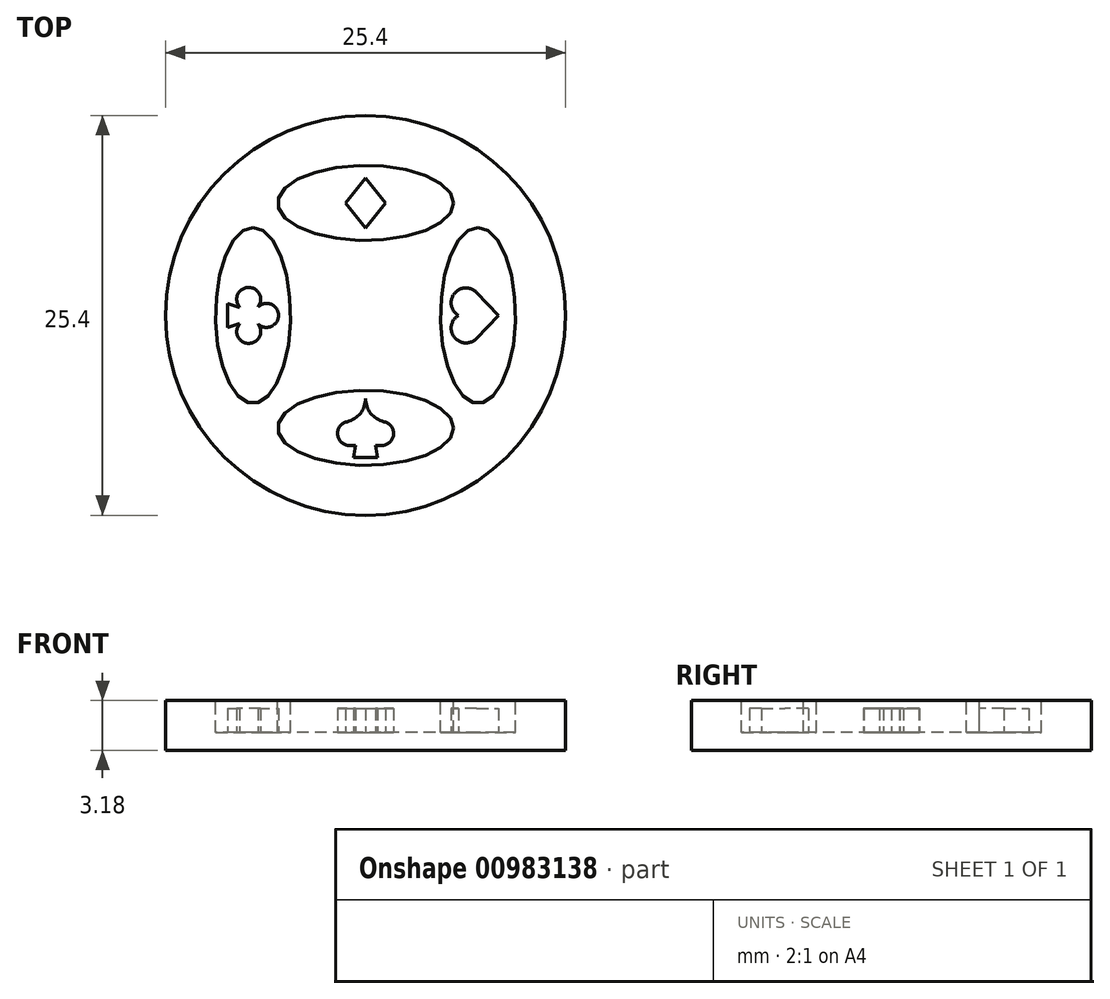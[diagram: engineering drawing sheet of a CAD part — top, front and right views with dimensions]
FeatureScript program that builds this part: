
annotation { "Feature Type Name" : "Feature", "Feature Type Description" : "" }
export const myFeature = defineFeature(function(context is Context, id is Id, definition is map)
    precondition{}
    {
        {
            var Q0;
            Q0=qCreatedBy(makeId("Top.planeOp"),FACE);
            var sketch = newSketch(context, id + "F0", { "sketchPlane" : qUnion([Q0])});
            skCircle(sketch, "E0", {"center": v(0, 0) * mm, "radius": 12.7 * mm});
            skSolve(sketch);
        }
        {
            var Q0;
            Q0 = qSketchRegion(id + "F0", true);
            extrude(context, id + "F1", {"entities" : qUnion([Q0]), "endBound" : BoundingType.SYMMETRIC, "depth" : 3.17 * mm, "offsetDistance" : 25.4 * mm});
        }
        {
            var Q0;
            Q0=makeQuery(id+"F1.opExtrude","CAP_FACE",FACE,{"disambiguationData":[OSD([sQuery(id+"F0.wireOp",EDGE,"E0")])],"isStart":false});
            var sketch = newSketch(context, id + "F2", { "sketchPlane" : qUnion([Q0])});
            skEllipse(sketch, "E1", {"center": v(0, 7.14) * mm, "majorRadius": 5.59 * mm, "minorRadius": 2.38 * mm, "majorAxis": v(1, 0)});
            skEllipse(sketch, "E2", {"center": v(7.14, 0) * mm, "majorRadius": 2.38 * mm, "minorRadius": 5.59 * mm, "majorAxis": v(1, 0)});
            skEllipse(sketch, "E3", {"center": v(0, -7.14) * mm, "majorRadius": 5.59 * mm, "minorRadius": 2.38 * mm, "majorAxis": v(1, 0)});
            skLineSegment(sketch, "E4", {"start": v(0, 4.76) * mm, "end": v(0, 9.52) * mm, "construction": true});
            skLineSegment(sketch, "E5", {"start": v(5.59, 7.14) * mm, "end": v(-5.59, 7.14) * mm, "construction": true});
            skPoint(sketch, "E6.endSnap0", {"position": v(-5.59, -7.14) * mm});
            skLineSegment(sketch, "E7", {"start": v(5.59, 7.14) * mm, "end": v(5.59, -7.14) * mm, "construction": true});
            skPoint(sketch, "E8.endSnap0", {"position": v(7.14, -5.59) * mm});
            skLineSegment(sketch, "E9", {"start": v(4.76, 0) * mm, "end": v(9.53, 0) * mm, "construction": true});
            skLineSegment(sketch, "E10", {"start": v(7.14, 5.59) * mm, "end": v(7.14, -5.59) * mm, "construction": true});
            skLineSegment(sketch, "E11", {"start": v(-5.59, -7.14) * mm, "end": v(5.59, -7.14) * mm, "construction": true});
            skLineSegment(sketch, "E12", {"start": v(0, -4.76) * mm, "end": v(0, -9.52) * mm, "construction": true});
            skEllipse(sketch, "E13", {"center": v(-7.14, 0) * mm, "majorRadius": 2.38 * mm, "minorRadius": 5.59 * mm, "majorAxis": v(1, 0)});
            skLineSegment(sketch, "E14", {"start": v(-7.14, 5.59) * mm, "end": v(-7.14, -5.59) * mm, "construction": true});
            skLineSegment(sketch, "E15", {"start": v(-4.76, 0) * mm, "end": v(-9.52, 0) * mm, "construction": true});
            skLineSegment(sketch, "E16", {"start": v(-7.14, 5.59) * mm, "end": v(7.14, 5.59) * mm, "construction": true});
            skLineSegment(sketch, "E17", {"start": v(0, 5.59) * mm, "end": v(0, 4.76) * mm, "construction": true});
            skLineSegment(sketch, "E18", {"start": v(5.59, 0) * mm, "end": v(4.76, 0) * mm, "construction": true});
            skSolve(sketch);
        }
        {
            var Q0;
            Q0 = qSketchRegion(id + "F2", true);
            extrude(context, id + "F3", {"entities" : qUnion([Q0]), "operationType" : NewBodyOperationType.REMOVE, "oppositeDirection" : true, "depth" : 2.03 * mm, "offsetDistance" : 25.4 * mm});
        }
        {
            var Q0;
            Q0=makeQuery(id+"F3.boolean.opBoolean","COPY",FACE,{"derivedFrom":makeQuery(id+"F3.opExtrude","CAP_FACE",FACE,{"disambiguationData":[OSD([sQuery(id+"F2.wireOp",EDGE,"E1")])],"isStart":false})});
            var sketch = newSketch(context, id + "F4", { "sketchPlane" : qUnion([Q0])});
            skPoint(sketch, "E19.firstSnap0", {"position": v(0, 4.76) * mm});
            skLineSegment(sketch, "E20", {"start": v(0, 5.56) * mm, "end": v(1.27, 7.14) * mm});
            skLineSegment(sketch, "E21", {"start": v(1.27, 7.14) * mm, "end": v(0, 8.73) * mm});
            skLineSegment(sketch, "E22", {"start": v(0, 8.73) * mm, "end": v(-1.27, 7.14) * mm});
            skLineSegment(sketch, "E23", {"start": v(-1.27, 7.14) * mm, "end": v(0, 5.56) * mm});
            skLineSegment(sketch, "E24", {"start": v(0, 4.76) * mm, "end": v(0, 5.56) * mm, "construction": true});
            skLineSegment(sketch, "E25", {"start": v(0, 9.52) * mm, "end": v(0, 8.73) * mm, "construction": true});
            skLineSegment(sketch, "E26", {"start": v(-1.27, 7.14) * mm, "end": v(1.27, 7.14) * mm, "construction": true});
            skArc(sketch, "E27", {"start": v(5.9, 0) * mm, "mid": v(5.64, -1.4) * mm, "end": v(7.06, -1.46) * mm});
            skArc(sketch, "E28", {"start": v(7.06, 1.46) * mm, "mid": v(5.64, 1.4) * mm, "end": v(5.9, 0) * mm});
            skLineSegment(sketch, "E29", {"start": v(7.06, -1.46) * mm, "end": v(8.46, 0) * mm});
            skLineSegment(sketch, "E30", {"start": v(8.46, 0) * mm, "end": v(7.06, 1.46) * mm});
            skLineSegment(sketch, "E31", {"start": v(8.46, 0) * mm, "end": v(9.53, 0) * mm, "construction": true});
            skLineSegment(sketch, "E32", {"start": v(5.9, 0) * mm, "end": v(4.76, 0) * mm, "construction": true});
            skArc(sketch, "E33", {"start": v(0, -5.27) * mm, "mid": v(0.33, -6.22) * mm, "end": v(1.19, -6.76) * mm});
            skArc(sketch, "E34", {"start": v(-1.19, -6.76) * mm, "mid": v(-0.33, -6.22) * mm, "end": v(0, -5.27) * mm});
            skArc(sketch, "E35", {"start": v(1.02, -8.26) * mm, "mid": v(1.77, -7.58) * mm, "end": v(1.19, -6.76) * mm});
            skArc(sketch, "E36", {"start": v(-1.19, -6.76) * mm, "mid": v(-1.77, -7.58) * mm, "end": v(-1.02, -8.26) * mm});
            skLineSegment(sketch, "E37", {"start": v(-1.02, -8.26) * mm, "end": v(1.02, -8.26) * mm});
            skLineSegment(sketch, "E38", {"start": v(0, -5.27) * mm, "end": v(0, -4.76) * mm, "construction": true});
            skLineSegment(sketch, "E39", {"start": v(0, -8.26) * mm, "end": v(0, -8.77) * mm, "construction": true});
            skLineSegment(sketch, "E40", {"start": v(-0.64, -8.26) * mm, "end": v(-0.76, -9.02) * mm});
            skLineSegment(sketch, "E41", {"start": v(-0.76, -9.02) * mm, "end": v(0.76, -9.02) * mm});
            skLineSegment(sketch, "E42", {"start": v(0.76, -9.02) * mm, "end": v(0.64, -8.26) * mm});
            skArc(sketch, "E43", {"start": v(-6.84, -0.52) * mm, "mid": v(-5.52, 0) * mm, "end": v(-6.84, 0.52) * mm});
            skArc(sketch, "E44", {"start": v(-7.99, -0.5) * mm, "mid": v(-7.43, -1.78) * mm, "end": v(-6.84, -0.52) * mm});
            skArc(sketch, "E45", {"start": v(-6.84, 0.52) * mm, "mid": v(-7.43, 1.78) * mm, "end": v(-7.99, 0.5) * mm});
            skLineSegment(sketch, "E46", {"start": v(-8.76, 0.76) * mm, "end": v(-8.76, -0.76) * mm});
            skLineSegment(sketch, "E47", {"start": v(-8.76, 0) * mm, "end": v(-9.52, 0) * mm, "construction": true});
            skLineSegment(sketch, "E48", {"start": v(-5.52, 0) * mm, "end": v(-4.76, 0) * mm, "construction": true});
            skPoint(sketch, "E48.startSnap0", {"position": v(-5.52, 0) * mm});
            skLineSegment(sketch, "E49", {"start": v(-7.42, 1.02) * mm, "end": v(-7.42, -1.02) * mm, "construction": true});
            skLineSegment(sketch, "E50", {"start": v(-6.29, 0) * mm, "end": v(-7.42, 0) * mm, "construction": true});
            skPoint(sketch, "E50.endSnap0", {"position": v(-7.42, 0) * mm});
            skLineSegment(sketch, "E51", {"start": v(-7.99, 0.5) * mm, "end": v(-7.99, -0.5) * mm, "construction": true});
            skLineSegment(sketch, "E52", {"start": v(-6.84, 0.52) * mm, "end": v(-6.84, -0.52) * mm, "construction": true});
            skLineSegment(sketch, "E53", {"start": v(-8.76, 0.76) * mm, "end": v(-7.99, 0.5) * mm});
            skLineSegment(sketch, "E54", {"start": v(-7.99, -0.5) * mm, "end": v(-8.76, -0.76) * mm});
            skSolve(sketch);
        }
        {
            var Q0;
            Q0 = qSketchRegion(id + "F4", true);
            extrude(context, id + "F5", {"entities" : qUnion([Q0]), "operationType" : NewBodyOperationType.ADD, "depth" : 1.52 * mm, "offsetDistance" : 25.4 * mm});
        }
    });
